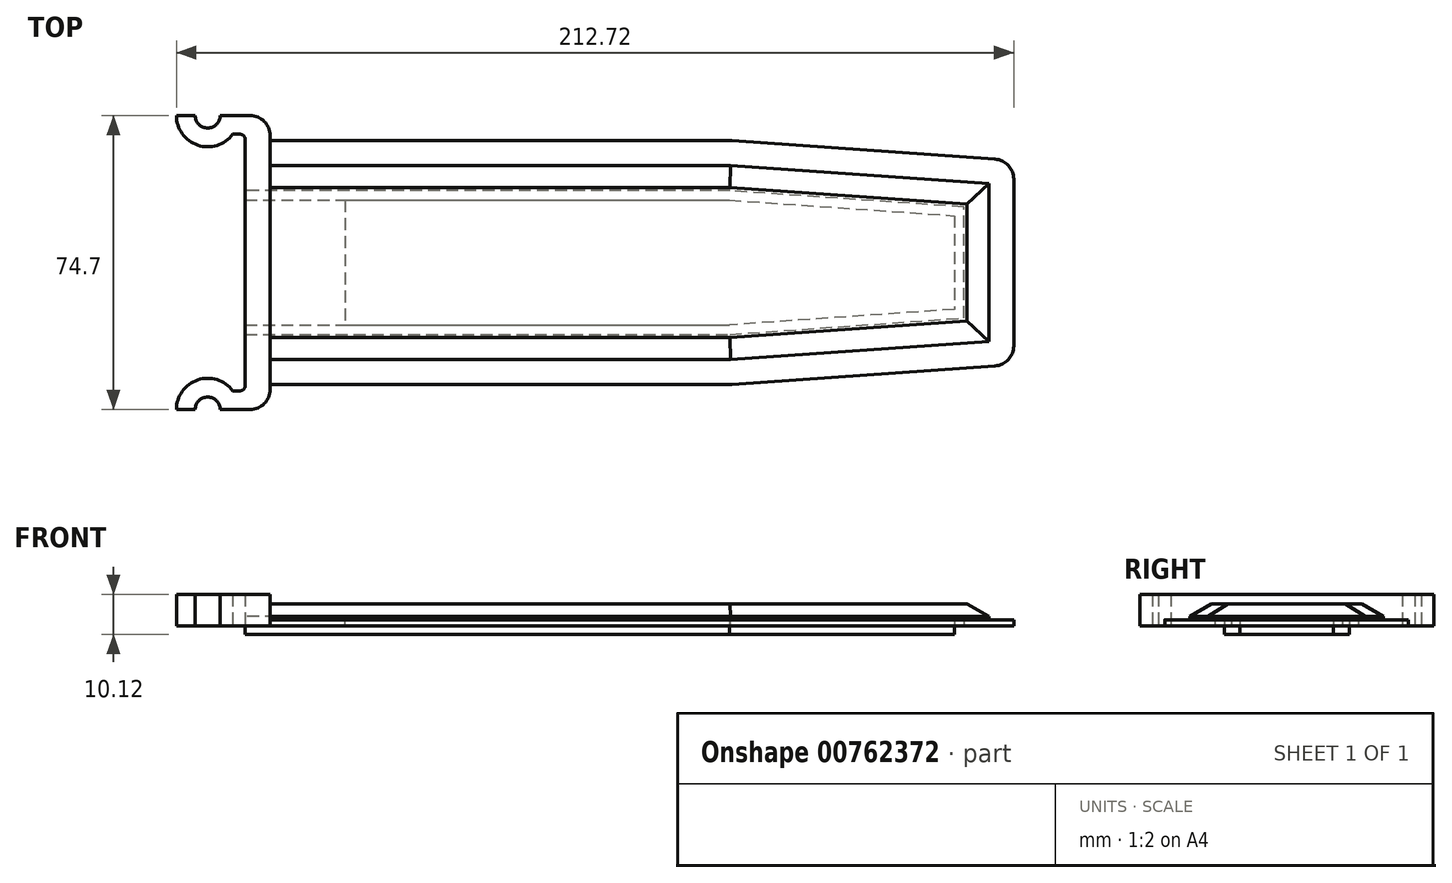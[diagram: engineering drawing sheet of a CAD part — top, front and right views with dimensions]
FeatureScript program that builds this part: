
annotation { "Feature Type Name" : "Feature", "Feature Type Description" : "" }
export const myFeature = defineFeature(function(context is Context, id is Id, definition is map)
    precondition{}
    {
        {
            var Q0;
            Q0=qCreatedBy(makeId("Top.planeOp"),FACE);
            var sketch = newSketch(context, id + "F0", { "sketchPlane" : qUnion([Q0])});
            skLineSegment(sketch, "E0.bottom", {"start": v(-88.9, 15.88) * mm, "end": v(31.75, 15.88) * mm});
            skLineSegment(sketch, "E0.top", {"start": v(-88.9, -15.88) * mm, "end": v(31.75, -15.88) * mm});
            skLineSegment(sketch, "E0.left", {"start": v(-88.9, 15.88) * mm, "end": v(-88.9, -15.88) * mm});
            skLineSegment(sketch, "E1", {"start": v(31.75, 15.88) * mm, "end": v(88.9, 11.88) * mm});
            skLineSegment(sketch, "E2", {"start": v(88.9, 11.88) * mm, "end": v(88.9, -11.88) * mm});
            skLineSegment(sketch, "E3", {"start": v(88.9, -11.88) * mm, "end": v(31.75, -15.88) * mm});
            skLineSegment(sketch, "E4", {"start": v(-88.9, 0) * mm, "end": v(88.9, 0) * mm, "construction": true});
            skSolve(sketch);
        }
        {
            var Q0;
            Q0 = qSketchRegion(id + "F0", true);
            extrude(context, id + "F1", {"entities" : qUnion([Q0]), "endBound" : BoundingType.SYMMETRIC, "depth" : 4.25 * mm, "offsetDistance" : 25.4 * mm});
        }
        {
            var Q0;
            Q0=qCreatedBy(makeId("Top.planeOp"),FACE);
            var sketch = newSketch(context, id + "F2", { "sketchPlane" : qUnion([Q0])});
            skLineSegment(sketch, "E5.0", {"start": v(31.83, 18.26) * mm, "end": v(-91.28, 18.26) * mm});
            skLineSegment(sketch, "E5.1", {"start": v(-91.28, -18.26) * mm, "end": v(31.83, -18.26) * mm});
            skLineSegment(sketch, "E5.2", {"start": v(31.83, -18.26) * mm, "end": v(91.28, -14.1) * mm});
            skLineSegment(sketch, "E5.3", {"start": v(-91.28, 18.26) * mm, "end": v(-91.28, -18.26) * mm, "construction": true});
            skLineSegment(sketch, "E5.4", {"start": v(91.28, -14.1) * mm, "end": v(91.28, 14.1) * mm});
            skLineSegment(sketch, "E5.5", {"start": v(91.28, 14.1) * mm, "end": v(31.83, 18.26) * mm});
            skLineSegment(sketch, "E6.0", {"start": v(103.98, 25.94) * mm, "end": v(32.28, 30.96) * mm});
            skLineSegment(sketch, "E6.2", {"start": v(-91.28, -30.96) * mm, "end": v(32.28, -30.96) * mm});
            skLineSegment(sketch, "E6.3", {"start": v(32.28, 30.96) * mm, "end": v(-91.28, 30.96) * mm});
            skLineSegment(sketch, "E6.4", {"start": v(32.28, -30.96) * mm, "end": v(103.98, -25.94) * mm});
            skLineSegment(sketch, "E6.5", {"start": v(103.98, -25.94) * mm, "end": v(103.98, 25.94) * mm});
            skLineSegment(sketch, "E7", {"start": v(-91.28, 18.26) * mm, "end": v(-91.28, 30.96) * mm});
            skLineSegment(sketch, "E8", {"start": v(-91.28, -18.26) * mm, "end": v(-91.28, -30.96) * mm});
            skSolve(sketch);
        }
        {
            var Q0;
            Q0 = qSketchRegion(id + "F2", true);
            var Q1;
            Q1=makeQuery(id+"F2.imprint","IMPRINT",FACE,{"disambiguationData":[TD([[makeQuery(id+"F2.imprint","IMPRINT",EDGE,{"derivedFrom":sQuery(id+"F2.wireOp",EDGE,"E5.0")}),-1.0]])]});
            extrude(context, id + "F3", {"entities" : qUnion([Q0, Q1]), "depth" : 1.59 * mm, "offsetDistance" : 25.4 * mm});
        }
        {
            var Q0;
            Q0=makeQuery(id+"F3.opExtrude","CAP_FACE",FACE,{"disambiguationData":[OSD([sQuery(id+"F2.wireOp",EDGE,"E5.0"),sQuery(id+"F2.wireOp",EDGE,"E5.1"),sQuery(id+"F2.wireOp",EDGE,"E5.2"),sQuery(id+"F2.wireOp",EDGE,"E5.4"),sQuery(id+"F2.wireOp",EDGE,"E5.5"),sQuery(id+"F2.wireOp",EDGE,"E6.0"),sQuery(id+"F2.wireOp",EDGE,"E6.2"),sQuery(id+"F2.wireOp",EDGE,"E6.3"),sQuery(id+"F2.wireOp",EDGE,"E6.4"),sQuery(id+"F2.wireOp",EDGE,"E6.5"),sQuery(id+"F2.wireOp",EDGE,"E7"),sQuery(id+"F2.wireOp",EDGE,"E8")])],"isStart":false});
            var sketch = newSketch(context, id + "F4", { "sketchPlane" : qUnion([Q0])});
            skLineSegment(sketch, "E9.0", {"start": v(31.83, -18.26) * mm, "end": v(91.28, -14.1) * mm});
            skLineSegment(sketch, "E10.0", {"start": v(-91.28, -18.26) * mm, "end": v(31.83, -18.26) * mm});
            skLineSegment(sketch, "E11.0", {"start": v(91.28, -14.1) * mm, "end": v(91.28, 14.1) * mm});
            skLineSegment(sketch, "E12.0", {"start": v(91.28, 14.1) * mm, "end": v(31.83, 18.26) * mm});
            skLineSegment(sketch, "E13.0", {"start": v(31.83, 18.26) * mm, "end": v(-91.28, 18.26) * mm});
            skLineSegment(sketch, "E14.0", {"start": v(32.06, 24.6) * mm, "end": v(-91.28, 24.6) * mm});
            skLineSegment(sketch, "E14.1", {"start": v(-91.28, -24.6) * mm, "end": v(32.06, -24.6) * mm});
            skLineSegment(sketch, "E14.2", {"start": v(32.06, -24.6) * mm, "end": v(97.63, -20.02) * mm});
            skLineSegment(sketch, "E14.3", {"start": v(97.63, -20.02) * mm, "end": v(97.63, 20.02) * mm});
            skLineSegment(sketch, "E14.4", {"start": v(97.63, 20.02) * mm, "end": v(32.06, 24.6) * mm});
            skLineSegment(sketch, "E15", {"start": v(-91.28, -24.6) * mm, "end": v(-91.28, -18.26) * mm});
            skLineSegment(sketch, "E16", {"start": v(-91.28, 18.26) * mm, "end": v(-91.28, 24.6) * mm});
            skSolve(sketch);
        }
        {
            var Q0;
            Q0 = qSketchRegion(id + "F4", true);
            extrude(context, id + "F5", {"entities" : qUnion([Q0]), "operationType" : NewBodyOperationType.ADD, "depth" : 0.8 * mm, "offsetDistance" : 25.4 * mm});
        }
        {
            var Q0;
            Q0=makeQuery(id+"F5.opExtrude","CAP_FACE",FACE,{"disambiguationData":[OSD([sQuery(id+"F4.wireOp",EDGE,"E9.0"),sQuery(id+"F4.wireOp",EDGE,"E10.0"),sQuery(id+"F4.wireOp",EDGE,"E11.0"),sQuery(id+"F4.wireOp",EDGE,"E12.0"),sQuery(id+"F4.wireOp",EDGE,"E13.0"),sQuery(id+"F4.wireOp",EDGE,"E14.0"),sQuery(id+"F4.wireOp",EDGE,"E14.1"),sQuery(id+"F4.wireOp",EDGE,"E14.2"),sQuery(id+"F4.wireOp",EDGE,"E14.3"),sQuery(id+"F4.wireOp",EDGE,"E14.4"),sQuery(id+"F4.wireOp",EDGE,"E15"),sQuery(id+"F4.wireOp",EDGE,"E16")])],"isStart":false});
            var sketch = newSketch(context, id + "F6", { "sketchPlane" : qUnion([Q0])});
            skLineSegment(sketch, "E17.0", {"start": v(-91.28, -24.6) * mm, "end": v(32.06, -24.6) * mm});
            skLineSegment(sketch, "E18.0", {"start": v(32.06, -24.6) * mm, "end": v(97.63, -20.02) * mm});
            skLineSegment(sketch, "E19.0", {"start": v(97.63, -20.02) * mm, "end": v(97.63, 20.02) * mm});
            skLineSegment(sketch, "E20.0", {"start": v(97.63, 20.02) * mm, "end": v(32.06, 24.6) * mm});
            skLineSegment(sketch, "E21.0", {"start": v(32.06, 24.6) * mm, "end": v(-91.28, 24.6) * mm});
            skLineSegment(sketch, "E22", {"start": v(-91.28, 24.6) * mm, "end": v(-91.28, -24.6) * mm});
            skSolve(sketch);
        }
        {
            var Q0;
            Q0 = qSketchRegion(id + "F6", true);
            extrude(context, id + "F7", {"entities" : qUnion([Q0]), "operationType" : NewBodyOperationType.ADD, "depth" : 3.17 * mm, "offsetDistance" : 25.4 * mm, "hasDraft" : true, "draftAngle" : 60 * degree, "draftPullDirection" : true});
        }
        {
            var Q0;
            Q0=makeQuery(id+"F3.opExtrude","SWEPT_EDGE",EDGE,{"disambiguationData":[OSD([sQuery(id+"F2.wireOp",EDGE,"E6.4"),sQuery(id+"F2.wireOp",EDGE,"E6.5")])]});
            var Q1;
            Q1=makeQuery(id+"F3.opExtrude","SWEPT_EDGE",EDGE,{"disambiguationData":[OSD([sQuery(id+"F2.wireOp",EDGE,"E6.0"),sQuery(id+"F2.wireOp",EDGE,"E6.5")])]});
            var Q2;
            Q2=makeQuery(id+"F3.opExtrude","SWEPT_EDGE",EDGE,{"disambiguationData":[OSD([sQuery(id+"F2.wireOp",EDGE,"E6.2"),sQuery(id+"F2.wireOp",EDGE,"E6.4")])]});
            var Q3;
            Q3=makeQuery(id+"F3.opExtrude","SWEPT_EDGE",EDGE,{"disambiguationData":[OSD([sQuery(id+"F2.wireOp",EDGE,"E6.0"),sQuery(id+"F2.wireOp",EDGE,"E6.3")])]});
            fillet(context, id + "F8", {"entities" : qUnion([Q0, Q1, Q2, Q3]), "radius" : 5.08 * mm, "tangentPropagation" : true, "allowEdgeOverflow" : false});
        }
        {
            var Q0;
            Q0=makeQuery(id+"F3.opExtrude","CAP_FACE",FACE,{"disambiguationData":[OSD([sQuery(id+"F2.wireOp",EDGE,"E5.0"),sQuery(id+"F2.wireOp",EDGE,"E5.1"),sQuery(id+"F2.wireOp",EDGE,"E5.2"),sQuery(id+"F2.wireOp",EDGE,"E5.4"),sQuery(id+"F2.wireOp",EDGE,"E5.5"),sQuery(id+"F2.wireOp",EDGE,"E6.0"),sQuery(id+"F2.wireOp",EDGE,"E6.2"),sQuery(id+"F2.wireOp",EDGE,"E6.3"),sQuery(id+"F2.wireOp",EDGE,"E6.4"),sQuery(id+"F2.wireOp",EDGE,"E6.5"),sQuery(id+"F2.wireOp",EDGE,"E7"),sQuery(id+"F2.wireOp",EDGE,"E8")])],"isStart":false});
            var sketch = newSketch(context, id + "F9", { "sketchPlane" : qUnion([Q0])});
            skLineSegment(sketch, "E23.bottom", {"start": v(-91.28, 30.96) * mm, "end": v(-85.78, 30.96) * mm});
            skLineSegment(sketch, "E23.top", {"start": v(-91.28, -30.96) * mm, "end": v(-85.78, -30.96) * mm});
            skLineSegment(sketch, "E23.left", {"start": v(-91.28, 30.96) * mm, "end": v(-91.28, -30.96) * mm});
            skLineSegment(sketch, "E23.right", {"start": v(-85.78, 30.96) * mm, "end": v(-85.78, -30.96) * mm});
            skSolve(sketch);
        }
        {
            var Q0;
            Q0 = qSketchRegion(id + "F9", true);
            var Q1;
            Q1=makeQuery(id+"F7.opExtrude","CAP_FACE",FACE,{"disambiguationData":[OSD([sQuery(id+"F6.wireOp",EDGE,"E17.0"),sQuery(id+"F6.wireOp",EDGE,"E18.0"),sQuery(id+"F6.wireOp",EDGE,"E19.0"),sQuery(id+"F6.wireOp",EDGE,"E20.0"),sQuery(id+"F6.wireOp",EDGE,"E21.0"),sQuery(id+"F6.wireOp",EDGE,"E22")])],"isStart":false});
            extrude(context, id + "F10", {"entities" : qUnion([Q0]), "operationType" : NewBodyOperationType.ADD, "endBound" : BoundingType.UP_TO_SURFACE, "depth" : 25.4 * mm, "endBoundEntityFace" : qUnion([Q1]), "offsetDistance" : 25.4 * mm});
        }
        {
            var Q0;
            Q0=makeQuery(id+"F1.opExtrude","SWEPT_FACE",FACE,{"disambiguationData":[OSD([sQuery(id+"F0.wireOp",EDGE,"E0.left")])]});
            var sketch = newSketch(context, id + "F11", { "sketchPlane" : qUnion([Q0])});
            skLineSegment(sketch, "E24.0.0", {"start": v(-15.87, -2.12) * mm, "end": v(15.88, -2.12) * mm});
            skLineSegment(sketch, "E24.0.1", {"start": v(15.88, -2.12) * mm, "end": v(15.88, 2.12) * mm});
            skLineSegment(sketch, "E24.0.2", {"start": v(15.88, 2.12) * mm, "end": v(-15.87, 2.12) * mm});
            skLineSegment(sketch, "E24.0.3", {"start": v(-15.88, 2.12) * mm, "end": v(-15.88, -2.12) * mm});
            skSolve(sketch);
        }
        {
            var Q0;
            Q0 = qSketchRegion(id + "F11", true);
            var Q1;
            Q1=makeQuery(id+"F10.boolean.opBoolean","MERGE",FACE,{"derivedFrom":[makeQuery(id+"F5.boolean.opBoolean","MERGE",FACE,{"derivedFrom":[makeQuery(id+"F3.opExtrude","SWEPT_FACE",FACE,{"disambiguationData":[OSD([sQuery(id+"F2.wireOp",EDGE,"E7")])]}),makeQuery(id+"F5.opExtrude","SWEPT_FACE",FACE,{"disambiguationData":[OSD([sQuery(id+"F4.wireOp",EDGE,"E16")])]})]}),makeQuery(id+"F5.boolean.opBoolean","MERGE",FACE,{"derivedFrom":[makeQuery(id+"F3.opExtrude","SWEPT_FACE",FACE,{"disambiguationData":[OSD([sQuery(id+"F2.wireOp",EDGE,"E8")])]}),makeQuery(id+"F5.opExtrude","SWEPT_FACE",FACE,{"disambiguationData":[OSD([sQuery(id+"F4.wireOp",EDGE,"E15")])]})]}),makeQuery(id+"F10.opExtrude","SWEPT_FACE",FACE,{"disambiguationData":[OSD([sQuery(id+"F9.wireOp",EDGE,"E23.left")])]})]});
            extrude(context, id + "F12", {"entities" : qUnion([Q0]), "operationType" : NewBodyOperationType.ADD, "endBound" : BoundingType.UP_TO_SURFACE, "depth" : 25.4 * mm, "endBoundEntityFace" : qUnion([Q1]), "offsetDistance" : 25.4 * mm});
        }
        {
            var Q0;
            Q0=qCreatedBy(makeId("Top.planeOp"),FACE);
            var sketch = newSketch(context, id + "F13", { "sketchPlane" : qUnion([Q0])});
            skArc(sketch, "E25", {"start": v(-91.3, 18.25) * mm, "mid": v(-91.9, 24.64) * mm, "end": v(-92.68, 31) * mm, "construction": true});
            skLineSegment(sketch, "E26", {"start": v(-91.28, 17.75) * mm, "end": v(-91.28, -17.75) * mm, "construction": true});
            skLineSegment(sketch, "E27", {"start": v(-92.68, 31) * mm, "end": v(-92.68, -31) * mm, "construction": true});
            skArc(sketch, "E28.trimOffspring", {"start": v(-92.68, -31) * mm, "mid": v(-91.9, -24.64) * mm, "end": v(-91.3, -18.25) * mm, "construction": true});
            skPoint(sketch, "E29.visualSharp", {"position": v(-91.28, 18) * mm});
            skArc(sketch, "E29.filletArc", {"start": v(-91.28, 17.75) * mm, "mid": v(-91.29, 18) * mm, "end": v(-91.3, 18.25) * mm, "construction": true});
            skPoint(sketch, "E30.visualSharp", {"position": v(-91.28, -18) * mm});
            skArc(sketch, "E30.filletArc", {"start": v(-91.3, -18.25) * mm, "mid": v(-91.29, -18) * mm, "end": v(-91.28, -17.75) * mm, "construction": true});
            skArc(sketch, "E31.0", {"start": v(-93.3, 18.1) * mm, "mid": v(-93.9, 24.49) * mm, "end": v(-94.68, 30.86) * mm, "construction": true});
            skArc(sketch, "E31.1", {"start": v(-94.66, -30.73) * mm, "mid": v(-93.9, -24.42) * mm, "end": v(-93.3, -18.1) * mm, "construction": true});
            skArc(sketch, "E31.2", {"start": v(-93.3, -18.1) * mm, "mid": v(-93.28, -17.92) * mm, "end": v(-93.28, -17.75) * mm, "construction": true});
            skLineSegment(sketch, "E31.3", {"start": v(-93.28, 17.75) * mm, "end": v(-93.28, -17.75) * mm, "construction": true});
            skArc(sketch, "E31.4", {"start": v(-93.28, 17.75) * mm, "mid": v(-93.28, 17.92) * mm, "end": v(-93.3, 18.1) * mm, "construction": true});
            skLineSegment(sketch, "E32", {"start": v(-92.68, -31) * mm, "end": v(-94.66, -30.73) * mm, "construction": true});
            skArc(sketch, "E33", {"start": v(-92.68, 31) * mm, "mid": v(-93.75, 32) * mm, "end": v(-94.68, 30.86) * mm, "construction": true});
            skArc(sketch, "E34", {"start": v(-94.66, -30.73) * mm, "mid": v(-93.8, -31.86) * mm, "end": v(-92.68, -31) * mm, "construction": true});
            skArc(sketch, "E35", {"start": v(-108.74, 37.35) * mm, "mid": v(-103.32, 29.82) * mm, "end": v(-94.46, 32.59) * mm});
            skArc(sketch, "E36", {"start": v(-103.98, 37.35) * mm, "mid": v(-100.8, 34.18) * mm, "end": v(-97.63, 37.35) * mm});
            skLineSegment(sketch, "E37", {"start": v(-91.28, 32.59) * mm, "end": v(-94.46, 32.59) * mm});
            skLineSegment(sketch, "E38", {"start": v(-84.93, 37.35) * mm, "end": v(-84.93, 0) * mm});
            skLineSegment(sketch, "E39", {"start": v(-84.93, 0) * mm, "end": v(-91.28, 0) * mm, "construction": true});
            skLineSegment(sketch, "E40", {"start": v(-91.28, 0) * mm, "end": v(-91.28, 32.59) * mm});
            skLineSegment(sketch, "E41", {"start": v(-108.74, 37.35) * mm, "end": v(-103.98, 37.35) * mm});
            skLineSegment(sketch, "E42.trimOffspring", {"start": v(-97.63, 37.35) * mm, "end": v(-84.93, 37.35) * mm});
            skLineSegment(sketch, "E43.MirrorCS", {"start": v(-84.93, -37.35) * mm, "end": v(-84.93, 0) * mm});
            skLineSegment(sketch, "E44.MirrorCS", {"start": v(-97.63, -37.35) * mm, "end": v(-84.93, -37.35) * mm});
            skArc(sketch, "E45.MirrorCS", {"start": v(-103.98, -37.35) * mm, "mid": v(-100.8, -34.18) * mm, "end": v(-97.63, -37.35) * mm});
            skLineSegment(sketch, "E46.MirrorCS", {"start": v(-108.74, -37.35) * mm, "end": v(-103.98, -37.35) * mm});
            skArc(sketch, "E47.MirrorCS", {"start": v(-108.74, -37.35) * mm, "mid": v(-103.32, -29.82) * mm, "end": v(-94.46, -32.59) * mm});
            skLineSegment(sketch, "E48.MirrorCS", {"start": v(-91.28, -32.59) * mm, "end": v(-94.46, -32.59) * mm});
            skLineSegment(sketch, "E49.MirrorCS", {"start": v(-91.28, 0) * mm, "end": v(-91.28, -32.59) * mm});
            skLineSegment(sketch, "E50", {"start": v(-100.8, 37.35) * mm, "end": v(-100.8, 29.41) * mm, "construction": true});
            skSolve(sketch);
        }
        {
            var Q0;
            Q0 = qSketchRegion(id + "F13", true);
            extrude(context, id + "F14", {"entities" : qUnion([Q0]), "operationType" : NewBodyOperationType.ADD, "depth" : 8 * mm, "offsetDistance" : 25.4 * mm});
        }
        {
            var Q0;
            Q0=makeQuery(id+"F14.boolean.opBoolean","MERGE",FACE,{"derivedFrom":[makeQuery(id+"F10.boolean.opBoolean","MERGE",FACE,{"derivedFrom":[makeQuery(id+"F5.boolean.opBoolean","MERGE",FACE,{"derivedFrom":[makeQuery(id+"F3.opExtrude","SWEPT_FACE",FACE,{"disambiguationData":[OSD([sQuery(id+"F2.wireOp",EDGE,"E7")])]}),makeQuery(id+"F5.opExtrude","SWEPT_FACE",FACE,{"disambiguationData":[OSD([sQuery(id+"F4.wireOp",EDGE,"E16")])]})]}),makeQuery(id+"F5.boolean.opBoolean","MERGE",FACE,{"derivedFrom":[makeQuery(id+"F3.opExtrude","SWEPT_FACE",FACE,{"disambiguationData":[OSD([sQuery(id+"F2.wireOp",EDGE,"E8")])]}),makeQuery(id+"F5.opExtrude","SWEPT_FACE",FACE,{"disambiguationData":[OSD([sQuery(id+"F4.wireOp",EDGE,"E15")])]})]}),makeQuery(id+"F10.opExtrude","SWEPT_FACE",FACE,{"disambiguationData":[OSD([sQuery(id+"F9.wireOp",EDGE,"E23.left")])]})]}),makeQuery(id+"F14.opExtrude","SWEPT_FACE",FACE,{"disambiguationData":[OSD([sQuery(id+"F13.wireOp",EDGE,"E40"),sQuery(id+"F13.wireOp",EDGE,"E49.MirrorCS")])]})]});
            var sketch = newSketch(context, id + "F15", { "sketchPlane" : qUnion([Q0])});
            skLineSegment(sketch, "E51.0", {"start": v(-18.26, 2.38) * mm, "end": v(-18.26, 0) * mm});
            skLineSegment(sketch, "E52.0", {"start": v(-18.26, 2.38) * mm, "end": v(18.26, 2.38) * mm});
            skLineSegment(sketch, "E53.0", {"start": v(18.26, 0) * mm, "end": v(18.26, 2.38) * mm});
            skLineSegment(sketch, "E54", {"start": v(-18.26, 0) * mm, "end": v(18.26, 0) * mm});
            skSolve(sketch);
        }
        {
            var Q0;
            Q0 = qSketchRegion(id + "F15", true);
            extrude(context, id + "F16", {"entities" : qUnion([Q0]), "operationType" : NewBodyOperationType.REMOVE, "oppositeDirection" : true, "depth" : 25.4 * mm, "offsetDistance" : 25.4 * mm});
        }
        {
            var Q0;
            Q0=makeQuery(id+"F14.opExtrude","SWEPT_EDGE",EDGE,{"disambiguationData":[OSD([sQuery(id+"F13.wireOp",EDGE,"E38"),sQuery(id+"F13.wireOp",EDGE,"E42.trimOffspring")])]});
            var Q1;
            Q1=makeQuery(id+"F14.opExtrude","SWEPT_EDGE",EDGE,{"disambiguationData":[OSD([sQuery(id+"F13.wireOp",EDGE,"E43.MirrorCS"),sQuery(id+"F13.wireOp",EDGE,"E44.MirrorCS")])]});
            fillet(context, id + "F17", {"entities" : qUnion([Q0, Q1]), "radius" : 5.08 * mm, "tangentPropagation" : true, "allowEdgeOverflow" : false});
        }
        {
            var Q0;
            Q0=makeQuery(id+"F14.opExtrude","SWEPT_EDGE",EDGE,{"disambiguationData":[OSD([sQuery(id+"F13.wireOp",EDGE,"E48.MirrorCS"),sQuery(id+"F13.wireOp",EDGE,"E49.MirrorCS")])]});
            var Q1;
            Q1=makeQuery(id+"F14.opExtrude","SWEPT_EDGE",EDGE,{"disambiguationData":[OSD([sQuery(id+"F13.wireOp",EDGE,"E37"),sQuery(id+"F13.wireOp",EDGE,"E40")])]});
            fillet(context, id + "F18", {"entities" : qUnion([Q0, Q1]), "radius" : 1.27 * mm, "tangentPropagation" : true, "allowEdgeOverflow" : false});
        }
    });
